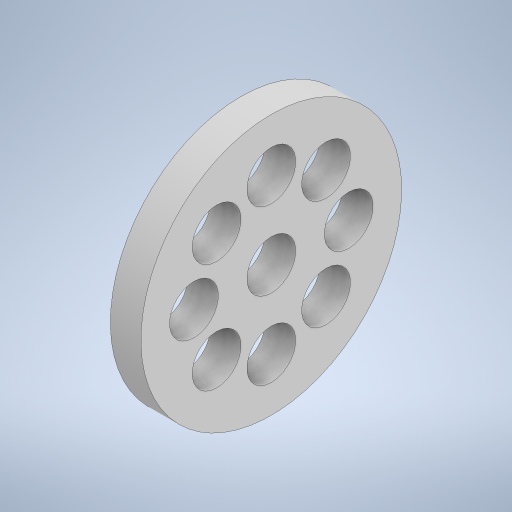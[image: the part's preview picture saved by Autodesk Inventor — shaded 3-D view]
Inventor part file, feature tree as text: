
AUTODESK INVENTOR PART (.ipt)
format: ipt  version: 2024.2 (Build 282272000, 272)  size: 399,872 bytes
history: native  units: in
note: dims shown in document units (in); Inventor stores cm internally (conversion verified against a paired STEP export)
features: extrude x1, sketch x1
ambient origin geometry x8: Origin, YZ Plane, XZ Plane, XY Plane, X Axis, Y Axis, Z Axis, Center Point
bodies: Solid1 (feature_tree)
feature tree (2):
  extrude  "Extrusion1"  Depth=0.185in
  sketch  "Sketch2"  dims[d0=1.5748in d1=0.2953in d2=0.185in d3=0.0in d4=1.5748in d6=360.0deg d8=3.1496in d10=360.0deg d12=0.2953in]
